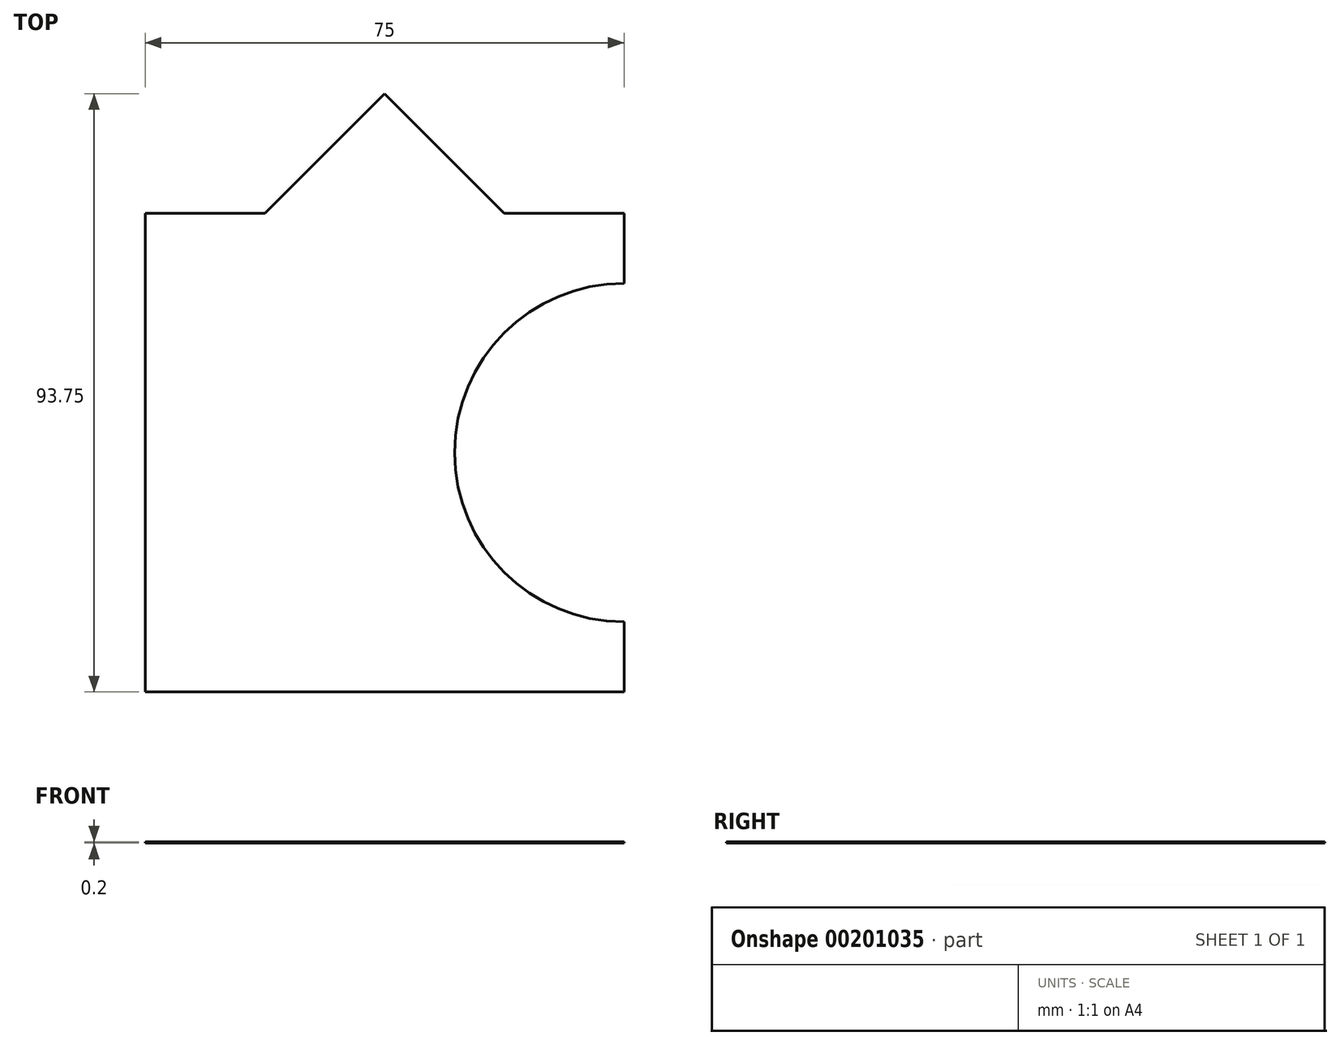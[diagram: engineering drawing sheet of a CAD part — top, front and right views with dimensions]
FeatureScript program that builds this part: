
annotation { "Feature Type Name" : "Feature", "Feature Type Description" : "" }
export const myFeature = defineFeature(function(context is Context, id is Id, definition is map)
    precondition{}
    {
        {
            var Q0;
            Q0=qCreatedBy(makeId("Top.planeOp"),FACE);
            var sketch = newSketch(context, id + "F0", { "sketchPlane" : qUnion([Q0])});
            skLineSegment(sketch, "E0.bottom", {"start": v(-37.5, 37.5) * mm, "end": v(37.5, 37.5) * mm});
            skLineSegment(sketch, "E0.top", {"start": v(-37.5, -37.5) * mm, "end": v(37.5, -37.5) * mm});
            skLineSegment(sketch, "E0.left", {"start": v(-37.5, 37.5) * mm, "end": v(-37.5, -37.5) * mm});
            skLineSegment(sketch, "E0.right", {"start": v(37.5, 37.5) * mm, "end": v(37.5, -37.5) * mm});
            skPoint(sketch, "E1", {"position": v(0, 37.5) * mm});
            skPoint(sketch, "E2", {"position": v(37.5, 0) * mm});
            skLineSegment(sketch, "E3", {"start": v(-37.5, 37.5) * mm, "end": v(0, 37.5) * mm, "construction": true});
            skPoint(sketch, "E4", {"position": v(-18.75, 37.5) * mm});
            skLineSegment(sketch, "E5", {"start": v(-18.75, 37.5) * mm, "end": v(0, 56.25) * mm});
            skLineSegment(sketch, "E6", {"start": v(-18.75, 37.5) * mm, "end": v(0, 37.5) * mm, "construction": true});
            skLineSegment(sketch, "E7", {"start": v(0, 56.25) * mm, "end": v(18.75, 37.5) * mm});
            skCircle(sketch, "E8", {"center": v(37.5, 0) * mm, "radius": 26.52 * mm});
            skLineSegment(sketch, "E9", {"start": v(37.5, 0) * mm, "end": v(64.02, 0) * mm, "construction": true});
            skSolve(sketch);
        }
        {
            var Q0;
            {var subQ0=sQuery(id+"F0.wireOp",EDGE,"E0.top");Q0=makeQuery(id+"F0.imprint","IMPRINT",FACE,{"disambiguationData":[TD([[makeQuery(id+"F0.imprint","IMPRINT",EDGE,{"derivedFrom":subQ0}),1.0]])]});}
            var Q1;
            {var subQ0=sQuery(id+"F0.wireOp",EDGE,"E5");Q1=makeQuery(id+"F0.imprint","IMPRINT",FACE,{"disambiguationData":[TD([[makeQuery(id+"F0.imprint","IMPRINT",EDGE,{"derivedFrom":subQ0}),-1.0]])]});}
            var Q2;
            {var subQ0=sQuery(id+"F0.wireOp",EDGE,"E8");var subQ1=sQuery(id+"F0.wireOp",EDGE,"E0.right");var subQ2=makeQuery(id+"F0.imprint","INTERSECT",VERTEX,{"disambiguationData":[OD(0.0)],"derivedFrom":[subQ1,subQ0]});Q2=makeQuery(id+"F0.imprint","IMPRINT",FACE,{"disambiguationData":[TD([[makeQuery(id+"F0.imprint","IMPRINT",EDGE,{"disambiguationData":[TD([[subQ2,-1.0]])],"derivedFrom":subQ1}),-1.0]])]});}
            var Q3;
            {var subQ0=sQuery(id+"F0.wireOp",EDGE,"E8");var subQ1=sQuery(id+"F0.wireOp",EDGE,"E0.right");var subQ2=makeQuery(id+"F0.imprint","INTERSECT",VERTEX,{"disambiguationData":[OD(0.0)],"derivedFrom":[subQ1,subQ0]});Q3=makeQuery(id+"F0.imprint","IMPRINT",FACE,{"disambiguationData":[TD([[makeQuery(id+"F0.imprint","IMPRINT",EDGE,{"disambiguationData":[TD([[subQ2,-1.0]])],"derivedFrom":subQ1}),1.0]])]});}
            extrude(context, id + "F1", {"entities" : qUnion([Q0, Q1, Q2, Q3]), "depth" : 0.2 * mm, "offsetDistance" : 25 * mm});
        }
    });
